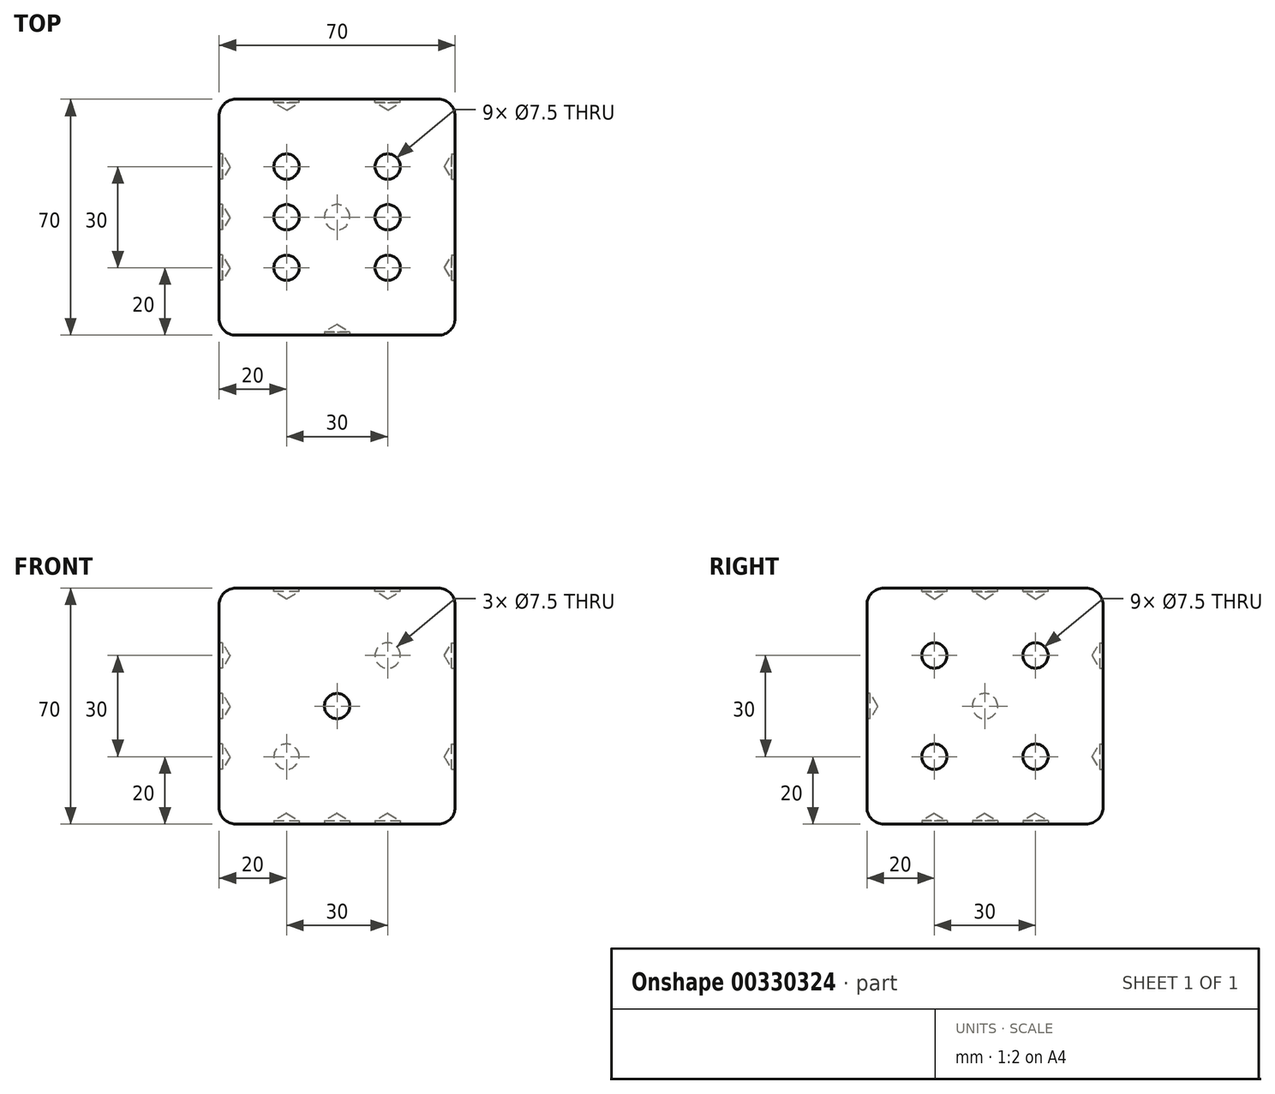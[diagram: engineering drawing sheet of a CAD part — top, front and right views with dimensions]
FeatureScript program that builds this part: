
annotation { "Feature Type Name" : "Feature", "Feature Type Description" : "" }
export const myFeature = defineFeature(function(context is Context, id is Id, definition is map)
    precondition{}
    {
        {
            var Q0;
            Q0=qCreatedBy(makeId("Front.planeOp"),FACE);
            var sketch = newSketch(context, id + "F0", { "sketchPlane" : qUnion([Q0])});
            skLineSegment(sketch, "E0.bottom", {"start": v(35, 35) * mm, "end": v(-35, 35) * mm});
            skLineSegment(sketch, "E0.top", {"start": v(35, -35) * mm, "end": v(-35, -35) * mm});
            skLineSegment(sketch, "E0.left", {"start": v(35, 35) * mm, "end": v(35, -35) * mm});
            skLineSegment(sketch, "E0.right", {"start": v(-35, 35) * mm, "end": v(-35, -35) * mm});
            skPoint(sketch, "E0.middle", {"position": v(0, 0) * mm});
            skSolve(sketch);
        }
        {
            var Q0;
            Q0 = qSketchRegion(id + "F0", true);
            extrude(context, id + "F1", {"entities" : qUnion([Q0]), "endBound" : BoundingType.SYMMETRIC, "depth" : 70 * mm});
        }
        {
            var Q0;
            Q0=makeQuery(id+"F1.opExtrude","CAP_EDGE",EDGE,{"disambiguationData":[OSD([sQuery(id+"F0.wireOp",EDGE,"E0.top")])],"isStart":true});
            fillet(context, id + "F2", {"entities" : qUnion([Q0]), "radius" : 5 * mm, "tangentPropagation" : true, "allowEdgeOverflow" : false});
        }
        {
            var Q0;
            Q0=makeQuery(id+"F1.opExtrude","CAP_EDGE",EDGE,{"disambiguationData":[OSD([sQuery(id+"F0.wireOp",EDGE,"E0.bottom")])],"isStart":true});
            fillet(context, id + "F3", {"entities" : qUnion([Q0]), "radius" : 5 * mm, "tangentPropagation" : true, "allowEdgeOverflow" : false});
        }
        {
            var Q0;
            Q0=makeQuery(id+"F1.opExtrude","CAP_EDGE",EDGE,{"disambiguationData":[OSD([sQuery(id+"F0.wireOp",EDGE,"E0.top")])],"isStart":false});
            fillet(context, id + "F4", {"entities" : qUnion([Q0]), "radius" : 5 * mm, "tangentPropagation" : true, "allowEdgeOverflow" : false});
        }
        {
            var Q0;
            Q0=makeQuery(id+"F1.opExtrude","SWEPT_EDGE",EDGE,{"disambiguationData":[OSD([sQuery(id+"F0.wireOp",EDGE,"E0.bottom"),sQuery(id+"F0.wireOp",EDGE,"E0.right")])]});
            fillet(context, id + "F5", {"entities" : qUnion([Q0]), "radius" : 5 * mm, "tangentPropagation" : true, "allowEdgeOverflow" : false});
        }
        {
            var Q0;
            Q0=makeQuery(id+"F1.opExtrude","CAP_EDGE",EDGE,{"disambiguationData":[OSD([sQuery(id+"F0.wireOp",EDGE,"E0.bottom")])],"isStart":false});
            fillet(context, id + "F6", {"entities" : qUnion([Q0]), "radius" : 5 * mm, "tangentPropagation" : true, "allowEdgeOverflow" : false});
        }
        {
            var Q0;
            Q0=makeQuery(id+"F1.opExtrude","SWEPT_EDGE",EDGE,{"disambiguationData":[OSD([sQuery(id+"F0.wireOp",EDGE,"E0.bottom"),sQuery(id+"F0.wireOp",EDGE,"E0.left")])]});
            fillet(context, id + "F7", {"entities" : qUnion([Q0]), "radius" : 5 * mm, "tangentPropagation" : true, "allowEdgeOverflow" : false});
        }
        {
            var Q0;
            Q0=makeQuery(id+"F1.opExtrude","CAP_FACE",FACE,{"disambiguationData":[OSD([sQuery(id+"F0.wireOp",EDGE,"E0.bottom"),sQuery(id+"F0.wireOp",EDGE,"E0.top"),sQuery(id+"F0.wireOp",EDGE,"E0.left"),sQuery(id+"F0.wireOp",EDGE,"E0.right")])],"isStart":false});
            var sketch = newSketch(context, id + "F8", { "sketchPlane" : qUnion([Q0])});
            skCircle(sketch, "E1", {"center": v(0, 0) * mm, "radius": 2.5 * mm});
            skSolve(sketch);
        }
        {
            var Q0;
            Q0=sQuery(id+"F8.wireOp",VERTEX,"E1.center");
            var Q1;
            Q1=makeQuery(id+"F1.opExtrude","SWEPT_BODY",BODY,{"disambiguationData":[OSD([sQuery(id+"F0.wireOp",EDGE,"E0.bottom"),sQuery(id+"F0.wireOp",EDGE,"E0.top"),sQuery(id+"F0.wireOp",EDGE,"E0.left"),sQuery(id+"F0.wireOp",EDGE,"E0.right")])]});
            hole(context, id + "F9", {"style" : HoleStyle.SIMPLE, "endStyle" : HoleEndStyle.BLIND, "holeDiameter" : 7.5 * mm, "holeDepth" : 1 * mm, "tappedDepth" : 12 * mm, "tapClearance" : 3, "locations" : qUnion([Q0]), "scope" : qUnion([Q1])});
        }
        {
            var Q0;
            Q0=makeQuery(id+"F1.opExtrude","SWEPT_FACE",FACE,{"disambiguationData":[OSD([sQuery(id+"F0.wireOp",EDGE,"E0.left")])]});
            var sketch = newSketch(context, id + "F10", { "sketchPlane" : qUnion([Q0])});
            skLineSegment(sketch, "E2", {"start": v(-30, 30) * mm, "end": v(30, -30) * mm});
            skLineSegment(sketch, "E3", {"start": v(-30, -30) * mm, "end": v(30, 30) * mm});
            skLineSegment(sketch, "E4", {"start": v(-30, 0) * mm, "end": v(30, 0) * mm});
            skLineSegment(sketch, "E5", {"start": v(0, -30) * mm, "end": v(0, 30) * mm});
            skPoint(sketch, "E5.endSnap0", {"position": v(0, 30) * mm});
            skLineSegment(sketch, "E6", {"start": v(-30, 15) * mm, "end": v(30, 15) * mm});
            skLineSegment(sketch, "E7", {"start": v(-30, -15) * mm, "end": v(30, -15) * mm});
            skCircle(sketch, "E8", {"center": v(-15, 15) * mm, "radius": 3.75 * mm});
            skCircle(sketch, "E9", {"center": v(15, 15) * mm, "radius": 3.75 * mm});
            skCircle(sketch, "E10", {"center": v(15, -15) * mm, "radius": 3.75 * mm});
            skCircle(sketch, "E11", {"center": v(-15, -15) * mm, "radius": 3.75 * mm});
            skSolve(sketch);
        }
        {
            var Q0;
            Q0=sQuery(id+"F10.wireOp",VERTEX,"E8.center");
            var Q1;
            Q1=sQuery(id+"F10.wireOp",VERTEX,"E9.center");
            var Q2;
            Q2=sQuery(id+"F10.wireOp",VERTEX,"E10.center");
            var Q3;
            Q3=sQuery(id+"F10.wireOp",VERTEX,"E11.center");
            var Q4;
            Q4=makeQuery(id+"F1.opExtrude","SWEPT_BODY",BODY,{"disambiguationData":[OSD([sQuery(id+"F0.wireOp",EDGE,"E0.bottom"),sQuery(id+"F0.wireOp",EDGE,"E0.top"),sQuery(id+"F0.wireOp",EDGE,"E0.left"),sQuery(id+"F0.wireOp",EDGE,"E0.right")])]});
            hole(context, id + "F11", {"style" : HoleStyle.SIMPLE, "endStyle" : HoleEndStyle.BLIND, "holeDiameter" : 7.5 * mm, "holeDepth" : 1 * mm, "tappedDepth" : 12 * mm, "tapClearance" : 3, "locations" : qUnion([Q0, Q1, Q2, Q3]), "scope" : qUnion([Q4])});
        }
        {
            var Q0;
            Q0=makeQuery(id+"F1.opExtrude","SWEPT_FACE",FACE,{"disambiguationData":[OSD([sQuery(id+"F0.wireOp",EDGE,"E0.bottom")])]});
            var sketch = newSketch(context, id + "F12", { "sketchPlane" : qUnion([Q0])});
            skLineSegment(sketch, "E12", {"start": v(-30, 0) * mm, "end": v(30, 0) * mm});
            skLineSegment(sketch, "E13", {"start": v(-30, 15) * mm, "end": v(30, 15) * mm});
            skLineSegment(sketch, "E14", {"start": v(-30, -15) * mm, "end": v(30, -15) * mm});
            skLineSegment(sketch, "E15", {"start": v(30, -30) * mm, "end": v(-30, 30) * mm});
            skLineSegment(sketch, "E16", {"start": v(-30, -30) * mm, "end": v(30, 30) * mm});
            skCircle(sketch, "E17", {"center": v(-15, 15) * mm, "radius": 3.75 * mm});
            skLineSegment(sketch, "E18", {"start": v(-15, 15) * mm, "end": v(-15, -15) * mm});
            skLineSegment(sketch, "E19", {"start": v(15, 15) * mm, "end": v(15, -15) * mm});
            skCircle(sketch, "E20", {"center": v(-15, -15) * mm, "radius": 3.75 * mm});
            skCircle(sketch, "E21", {"center": v(15, 15) * mm, "radius": 3.75 * mm});
            skCircle(sketch, "E22", {"center": v(15, -15) * mm, "radius": 3.75 * mm});
            skCircle(sketch, "E23", {"center": v(-15, 0) * mm, "radius": 3.75 * mm});
            skCircle(sketch, "E24", {"center": v(15, 0) * mm, "radius": 3.75 * mm});
            skSolve(sketch);
        }
        {
            var Q0;
            Q0=sQuery(id+"F12.wireOp",VERTEX,"E17.center");
            var Q1;
            Q1=sQuery(id+"F12.wireOp",VERTEX,"E21.center");
            var Q2;
            Q2=sQuery(id+"F12.wireOp",VERTEX,"E24.center");
            var Q3;
            Q3=sQuery(id+"F12.wireOp",VERTEX,"E19.end");
            var Q4;
            Q4=sQuery(id+"F12.wireOp",VERTEX,"E20.center");
            var Q5;
            Q5=sQuery(id+"F12.wireOp",VERTEX,"E23.center");
            var Q6;
            Q6=makeQuery(id+"F1.opExtrude","SWEPT_BODY",BODY,{"disambiguationData":[OSD([sQuery(id+"F0.wireOp",EDGE,"E0.bottom"),sQuery(id+"F0.wireOp",EDGE,"E0.top"),sQuery(id+"F0.wireOp",EDGE,"E0.left"),sQuery(id+"F0.wireOp",EDGE,"E0.right")])]});
            hole(context, id + "F13", {"style" : HoleStyle.SIMPLE, "endStyle" : HoleEndStyle.BLIND, "holeDiameter" : 7.5 * mm, "holeDepth" : 1 * mm, "tappedDepth" : 12 * mm, "tapClearance" : 3, "locations" : qUnion([Q0, Q1, Q2, Q3, Q4, Q5]), "scope" : qUnion([Q6])});
        }
        {
            var Q0;
            Q0=makeQuery(id+"F1.opExtrude","SWEPT_FACE",FACE,{"disambiguationData":[OSD([sQuery(id+"F0.wireOp",EDGE,"E0.right")])]});
            var sketch = newSketch(context, id + "F14", { "sketchPlane" : qUnion([Q0])});
            skLineSegment(sketch, "E25", {"start": v(-30, -30) * mm, "end": v(30, 30) * mm});
            skLineSegment(sketch, "E26", {"start": v(30, 30) * mm, "end": v(-30, 30) * mm});
            skLineSegment(sketch, "E27", {"start": v(-30, 30) * mm, "end": v(30, -30) * mm});
            skLineSegment(sketch, "E28", {"start": v(0, -30) * mm, "end": v(0, 30) * mm});
            skLineSegment(sketch, "E29", {"start": v(15, -30) * mm, "end": v(15, 30) * mm});
            skLineSegment(sketch, "E30", {"start": v(-15, -30) * mm, "end": v(-15, 30) * mm});
            skCircle(sketch, "E31", {"center": v(-15, -15) * mm, "radius": 3.75 * mm});
            skCircle(sketch, "E32", {"center": v(0, 0) * mm, "radius": 3.75 * mm});
            skCircle(sketch, "E33", {"center": v(-15, 15) * mm, "radius": 3.75 * mm});
            skCircle(sketch, "E34", {"center": v(15, 15) * mm, "radius": 3.75 * mm});
            skCircle(sketch, "E35", {"center": v(15, -15) * mm, "radius": 3.75 * mm});
            skSolve(sketch);
        }
        {
            var Q0;
            Q0=sQuery(id+"F14.wireOp",VERTEX,"E31.center");
            var Q1;
            Q1=sQuery(id+"F14.wireOp",VERTEX,"E33.center");
            var Q2;
            Q2=sQuery(id+"F14.wireOp",VERTEX,"E32.center");
            var Q3;
            Q3=sQuery(id+"F14.wireOp",VERTEX,"E34.center");
            var Q4;
            Q4=sQuery(id+"F14.wireOp",VERTEX,"E35.center");
            var Q5;
            Q5=makeQuery(id+"F1.opExtrude","SWEPT_BODY",BODY,{"disambiguationData":[OSD([sQuery(id+"F0.wireOp",EDGE,"E0.bottom"),sQuery(id+"F0.wireOp",EDGE,"E0.top"),sQuery(id+"F0.wireOp",EDGE,"E0.left"),sQuery(id+"F0.wireOp",EDGE,"E0.right")])]});
            hole(context, id + "F15", {"style" : HoleStyle.SIMPLE, "endStyle" : HoleEndStyle.BLIND, "holeDiameter" : 7.5 * mm, "holeDepth" : 1 * mm, "tappedDepth" : 12 * mm, "tapClearance" : 3, "locations" : qUnion([Q0, Q1, Q2, Q3, Q4]), "scope" : qUnion([Q5])});
        }
        {
            var Q0;
            Q0=makeQuery(id+"F1.opExtrude","SWEPT_FACE",FACE,{"disambiguationData":[OSD([sQuery(id+"F0.wireOp",EDGE,"E0.top")])]});
            var sketch = newSketch(context, id + "F16", { "sketchPlane" : qUnion([Q0])});
            skLineSegment(sketch, "E36", {"start": v(30, -30) * mm, "end": v(-30, 30) * mm});
            skLineSegment(sketch, "E37", {"start": v(-30, 30) * mm, "end": v(30, 30) * mm});
            skLineSegment(sketch, "E38", {"start": v(30, 30) * mm, "end": v(-30, -30) * mm});
            skLineSegment(sketch, "E39", {"start": v(-30, 0) * mm, "end": v(30, 0) * mm});
            skLineSegment(sketch, "E40", {"start": v(30, 0) * mm, "end": v(30, -30) * mm});
            skLineSegment(sketch, "E41", {"start": v(30, -15) * mm, "end": v(-30, -15) * mm});
            skLineSegment(sketch, "E42", {"start": v(-30, 15) * mm, "end": v(30, 15) * mm});
            skCircle(sketch, "E43", {"center": v(15, -15) * mm, "radius": 3.75 * mm});
            skCircle(sketch, "E44", {"center": v(0, 0) * mm, "radius": 3.75 * mm});
            skCircle(sketch, "E45", {"center": v(-15, 15) * mm, "radius": 3.75 * mm});
            skSolve(sketch);
        }
        {
            var Q0;
            Q0=sQuery(id+"F16.wireOp",VERTEX,"E43.center");
            var Q1;
            Q1=sQuery(id+"F16.wireOp",VERTEX,"E44.center");
            var Q2;
            Q2=sQuery(id+"F16.wireOp",VERTEX,"E45.center");
            var Q3;
            Q3=makeQuery(id+"F1.opExtrude","SWEPT_BODY",BODY,{"disambiguationData":[OSD([sQuery(id+"F0.wireOp",EDGE,"E0.bottom"),sQuery(id+"F0.wireOp",EDGE,"E0.top"),sQuery(id+"F0.wireOp",EDGE,"E0.left"),sQuery(id+"F0.wireOp",EDGE,"E0.right")])]});
            hole(context, id + "F17", {"style" : HoleStyle.SIMPLE, "endStyle" : HoleEndStyle.BLIND, "holeDiameter" : 7.5 * mm, "holeDepth" : 1 * mm, "tappedDepth" : 12 * mm, "tapClearance" : 3, "locations" : qUnion([Q0, Q1, Q2]), "scope" : qUnion([Q3])});
        }
        {
            var Q0;
            Q0=makeQuery(id+"F1.opExtrude","CAP_FACE",FACE,{"disambiguationData":[OSD([sQuery(id+"F0.wireOp",EDGE,"E0.bottom"),sQuery(id+"F0.wireOp",EDGE,"E0.top"),sQuery(id+"F0.wireOp",EDGE,"E0.left"),sQuery(id+"F0.wireOp",EDGE,"E0.right")])],"isStart":true});
            var sketch = newSketch(context, id + "F18", { "sketchPlane" : qUnion([Q0])});
            skLineSegment(sketch, "E46", {"start": v(-30, 30) * mm, "end": v(30, -30) * mm});
            skLineSegment(sketch, "E47", {"start": v(30, -30) * mm, "end": v(-30, -30) * mm});
            skLineSegment(sketch, "E48", {"start": v(30, 30) * mm, "end": v(-30, -30) * mm});
            skLineSegment(sketch, "E49", {"start": v(-30, 0) * mm, "end": v(30, 0) * mm});
            skLineSegment(sketch, "E50", {"start": v(30, 15) * mm, "end": v(-30, 15) * mm});
            skLineSegment(sketch, "E51", {"start": v(-30, -15) * mm, "end": v(30, -15) * mm});
            skCircle(sketch, "E52", {"center": v(-15, 15) * mm, "radius": 3.75 * mm});
            skCircle(sketch, "E53", {"center": v(15, -15) * mm, "radius": 3.75 * mm});
            skSolve(sketch);
        }
        {
            var Q0;
            Q0=sQuery(id+"F18.wireOp",VERTEX,"E52.center");
            var Q1;
            Q1=sQuery(id+"F18.wireOp",VERTEX,"E53.center");
            var Q2;
            Q2=makeQuery(id+"F1.opExtrude","SWEPT_BODY",BODY,{"disambiguationData":[OSD([sQuery(id+"F0.wireOp",EDGE,"E0.bottom"),sQuery(id+"F0.wireOp",EDGE,"E0.top"),sQuery(id+"F0.wireOp",EDGE,"E0.left"),sQuery(id+"F0.wireOp",EDGE,"E0.right")])]});
            hole(context, id + "F19", {"style" : HoleStyle.SIMPLE, "endStyle" : HoleEndStyle.BLIND, "holeDiameter" : 7.5 * mm, "holeDepth" : 1 * mm, "tappedDepth" : 12 * mm, "tapClearance" : 3, "locations" : qUnion([Q0, Q1]), "scope" : qUnion([Q2])});
        }
    });
